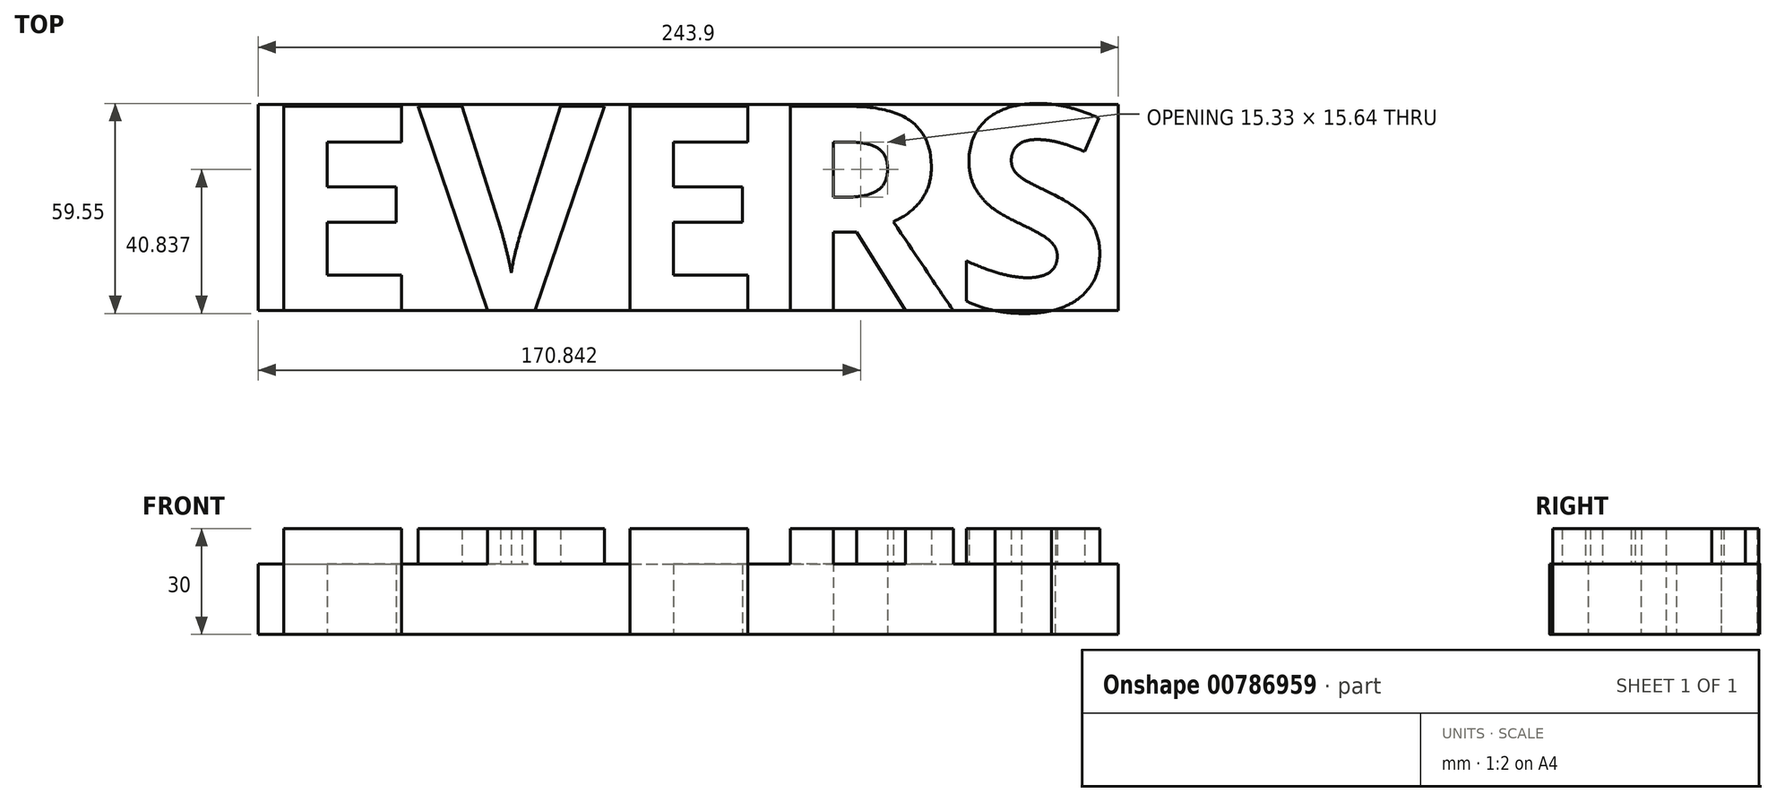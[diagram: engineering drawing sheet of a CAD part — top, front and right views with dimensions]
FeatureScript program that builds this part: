
annotation { "Feature Type Name" : "Feature", "Feature Type Description" : "" }
export const myFeature = defineFeature(function(context is Context, id is Id, definition is map)
    precondition{}
    {
        {
            var Q0;
            Q0=qCreatedBy(makeId("Top.planeOp"),FACE);
            var sketch = newSketch(context, id + "F0", { "sketchPlane" : qUnion([Q0])});
            skLineSegment(sketch, "E0.bottom", {"start": v(0, 34.85) * mm, "end": v(243.9, 34.85) * mm});
            skLineSegment(sketch, "E0.top", {"start": v(0, -23.57) * mm, "end": v(243.9, -23.57) * mm});
            skLineSegment(sketch, "E0.left", {"start": v(0, 34.85) * mm, "end": v(0, -23.57) * mm});
            skLineSegment(sketch, "E0.right", {"start": v(243.9, 34.85) * mm, "end": v(243.9, -23.57) * mm});
            skText(sketch, "E1", { "text": "EVERS", "fontName": "OpenSans-Bold.ttf"});
            const initialGuessF0  = {"E1": [0, -0.02357, 1, 0, 0.05842]};
            skSetInitialGuess(sketch, initialGuessF0);
            skSolve(sketch);
        }
        {
            var Q0;
            {var subQ1=sQuery(id+"F0.wireOp",EDGE,"E1.sketch_text.stroke-1");var subQ2=sQuery(id+"F0.wireOp",EDGE,"E0.top");var subQ11=makeQuery(id+"F0.imprint","IMPRINT",EDGE,{"derivedFrom":subQ1});var subQ20=sQuery(id+"F0.wireOp",EDGE,"E1.sketch_text.stroke-41");var subQ21=makeQuery(id+"F0.imprint","IMPRINT",EDGE,{"derivedFrom":subQ20});var subQ34=sQuery(id+"F0.wireOp",EDGE,"E1.sketch_text.stroke-54");var subQ35=makeQuery(id+"F0.imprint","INTERSECT",VERTEX,{"derivedFrom":[subQ2,subQ34]});var subQ38=makeQuery(id+"F0.imprint","IMPRINT",EDGE,{"disambiguationData":[TD([[subQ35,1.0]])],"derivedFrom":subQ2});var subQ40=sQuery(id+"F0.wireOp",EDGE,"E1.sketch_text.stroke-69");var subQ41=sQuery(id+"F0.wireOp",EDGE,"E0.bottom");var subQ42=makeQuery(id+"F0.imprint","INTERSECT",VERTEX,{"derivedFrom":[subQ41,subQ40]});var subQ45=makeQuery(id+"F0.imprint","IMPRINT",EDGE,{"disambiguationData":[TD([[subQ42,1.0]])],"derivedFrom":subQ41});var subQ48=sQuery(id+"F0.wireOp",EDGE,"E1.sketch_text.stroke-53");var subQ53=sQuery(id+"F0.wireOp",EDGE,"E0.right");var subQ55=makeQuery(id+"F0.imprint","IMPRINT",EDGE,{"derivedFrom":subQ48});var subQ74=sQuery(id+"F0.wireOp",EDGE,"E1.sketch_text.stroke-23");var subQ75=makeQuery(id+"F0.imprint","IMPRINT",EDGE,{"derivedFrom":subQ74});var subQ81=sQuery(id+"F0.wireOp",EDGE,"E0.left");var subQ90=makeQuery(id+"F0.imprint","IMPRINT",EDGE,{"derivedFrom":sQuery(id+"F0.wireOp",EDGE,"E1.sketch_text.stroke-12")});Q0=qUnion([makeQuery(id+"F0.imprint","IMPRINT",FACE,{"disambiguationData":[TD([[subQ55,-1.0]])]}),makeQuery(id+"F0.imprint","IMPRINT",FACE,{"disambiguationData":[TD([[subQ75,-1.0]])]}),makeQuery(id+"F0.imprint","IMPRINT",FACE,{"disambiguationData":[TD([[subQ90,-1.0]])]}),makeQuery(id+"F0.imprint","IMPRINT",FACE,{"disambiguationData":[TD([[makeQuery(id+"F0.imprint","IMPRINT",EDGE,{"derivedFrom":subQ81}),1.0]])]}),makeQuery(id+"F0.imprint","IMPRINT",FACE,{"disambiguationData":[TD([[makeQuery(id+"F0.imprint","IMPRINT",EDGE,{"derivedFrom":subQ53}),-1.0]])]}),makeQuery(id+"F0.imprint","IMPRINT",FACE,{"disambiguationData":[TD([[subQ21,1.0]])]}),makeQuery(id+"F0.imprint","IMPRINT",FACE,{"disambiguationData":[TD([[subQ45,1.0]])]}),makeQuery(id+"F0.imprint","IMPRINT",FACE,{"disambiguationData":[TD([[subQ38,-1.0]])]}),makeQuery(id+"F0.imprint","IMPRINT",FACE,{"disambiguationData":[TD([[makeQuery(id+"F0.imprint","IMPRINT",EDGE,{"derivedFrom":sQuery(id+"F0.wireOp",EDGE,"E1.sketch_text.stroke-34")}),-1.0]])]}),makeQuery(id+"F0.imprint","IMPRINT",FACE,{"disambiguationData":[TD([[subQ11,-1.0]])]})]);}
            extrude(context, id + "F1", {"entities" : qUnion([Q0]), "depth" : 20 * mm, "offsetDistance" : 25.4 * mm});
        }
        {
            var Q0;
            {var subQ0=sQuery(id+"F0.wireOp",EDGE,"E1.sketch_text.stroke-1");Q0=makeQuery(id+"F0.imprint","IMPRINT",FACE,{"disambiguationData":[TD([[makeQuery(id+"F0.imprint","IMPRINT",EDGE,{"derivedFrom":subQ0}),-1.0]])]});}
            var Q1;
            Q1=makeQuery(id+"F0.imprint","IMPRINT",FACE,{"disambiguationData":[TD([[makeQuery(id+"F0.imprint","IMPRINT",EDGE,{"derivedFrom":sQuery(id+"F0.wireOp",EDGE,"E1.sketch_text.stroke-12")}),-1.0]])]});
            var Q2;
            {var subQ0=sQuery(id+"F0.wireOp",EDGE,"E1.sketch_text.stroke-23");Q2=makeQuery(id+"F0.imprint","IMPRINT",FACE,{"disambiguationData":[TD([[makeQuery(id+"F0.imprint","IMPRINT",EDGE,{"derivedFrom":subQ0}),-1.0]])]});}
            var Q3;
            Q3=makeQuery(id+"F0.imprint","IMPRINT",FACE,{"disambiguationData":[TD([[makeQuery(id+"F0.imprint","IMPRINT",EDGE,{"derivedFrom":sQuery(id+"F0.wireOp",EDGE,"E1.sketch_text.stroke-34")}),-1.0]])]});
            var Q4;
            {var subQ7=sQuery(id+"F0.wireOp",EDGE,"E1.sketch_text.stroke-53");Q4=makeQuery(id+"F0.imprint","IMPRINT",FACE,{"disambiguationData":[TD([[makeQuery(id+"F0.imprint","IMPRINT",EDGE,{"derivedFrom":subQ7}),-1.0]])]});}
            extrude(context, id + "F2", {"entities" : qUnion([Q0, Q1, Q2, Q3, Q4]), "operationType" : NewBodyOperationType.ADD, "depth" : 30 * mm, "offsetDistance" : 25 * mm});
        }
    });
